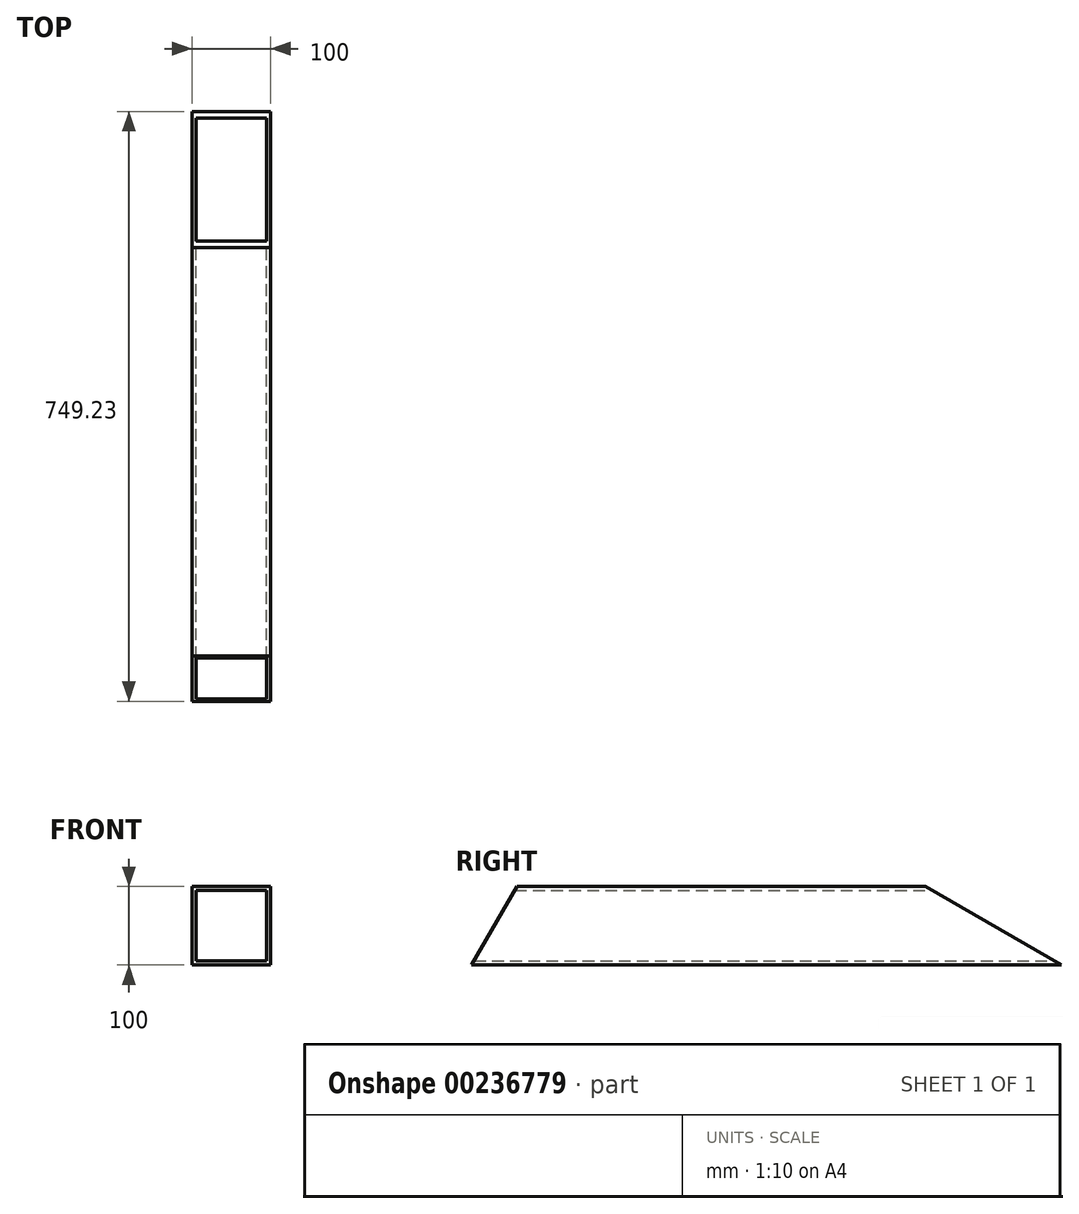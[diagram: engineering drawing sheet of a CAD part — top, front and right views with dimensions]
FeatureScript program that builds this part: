
annotation { "Feature Type Name" : "Feature", "Feature Type Description" : "" }
export const myFeature = defineFeature(function(context is Context, id is Id, definition is map)
    precondition{}
    {
        {
            var Q0;
            Q0=qCreatedBy(makeId("Front.planeOp"),FACE);
            var sketch = newSketch(context, id + "F0", { "sketchPlane" : qUnion([Q0])});
            skLineSegment(sketch, "E0.bottom", {"start": v(0, 0) * mm, "end": v(100, 0) * mm});
            skLineSegment(sketch, "E0.top", {"start": v(0, 100) * mm, "end": v(100, 100) * mm});
            skLineSegment(sketch, "E0.left", {"start": v(0, 0) * mm, "end": v(0, 100) * mm});
            skLineSegment(sketch, "E0.right", {"start": v(100, 0) * mm, "end": v(100, 100) * mm});
            skLineSegment(sketch, "E1.bottom", {"start": v(5, 95) * mm, "end": v(95, 95) * mm});
            skLineSegment(sketch, "E1.top", {"start": v(5, 5) * mm, "end": v(95, 5) * mm});
            skLineSegment(sketch, "E1.left", {"start": v(5, 95) * mm, "end": v(5, 5) * mm});
            skLineSegment(sketch, "E1.right", {"start": v(95, 95) * mm, "end": v(95, 5) * mm});
            skSolve(sketch);
        }
        {
            var Q0;
            Q0=makeQuery(id+"F0.imprint","IMPRINT",FACE,{"disambiguationData":[TD([[makeQuery(id+"F0.imprint","IMPRINT",EDGE,{"derivedFrom":sQuery(id+"F0.wireOp",EDGE,"E0.bottom")}),1.0]])]});
            extrude(context, id + "F1", {"entities" : qUnion([Q0]), "depth" : 750 * mm, "offsetDistance" : 25 * mm});
        }
        {
            var Q0;
            Q0=makeQuery(id+"F1.opExtrude","SWEPT_FACE",FACE,{"disambiguationData":[OSD([sQuery(id+"F0.wireOp",EDGE,"E0.right")])]});
            var sketch = newSketch(context, id + "F2", { "sketchPlane" : qUnion([Q0])});
            skLineSegment(sketch, "E2", {"start": v(-755, 120) * mm, "end": v(-679.94, 120) * mm});
            skLineSegment(sketch, "E3", {"start": v(-679.94, 120) * mm, "end": v(-755, -10) * mm});
            skLineSegment(sketch, "E4", {"start": v(-755, -10) * mm, "end": v(-755, 120) * mm});
            skSolve(sketch);
        }
        {
            var Q0;
            Q0 = qSketchRegion(id + "F2", true);
            extrude(context, id + "F3", {"entities" : qUnion([Q0]), "operationType" : NewBodyOperationType.REMOVE, "endBound" : BoundingType.THROUGH_ALL, "oppositeDirection" : true, "depth" : 25 * mm, "offsetDistance" : 25 * mm});
        }
        {
            var Q0;
            Q0=makeQuery(id+"F1.opExtrude","SWEPT_FACE",FACE,{"disambiguationData":[OSD([sQuery(id+"F0.wireOp",EDGE,"E0.right")])]});
            var sketch = newSketch(context, id + "F4", { "sketchPlane" : qUnion([Q0])});
            skLineSegment(sketch, "E5", {"start": v(-197.54, 114.15) * mm, "end": v(0.14, 0.02) * mm});
            skLineSegment(sketch, "E6", {"start": v(0.14, 0.02) * mm, "end": v(0.14, 114.15) * mm});
            skLineSegment(sketch, "E7", {"start": v(0.14, 114.15) * mm, "end": v(-197.54, 114.15) * mm});
            skSolve(sketch);
        }
        {
            var Q0;
            Q0 = qSketchRegion(id + "F4", true);
            extrude(context, id + "F5", {"entities" : qUnion([Q0]), "operationType" : NewBodyOperationType.REMOVE, "endBound" : BoundingType.THROUGH_ALL, "oppositeDirection" : true, "depth" : 25 * mm, "offsetDistance" : 25 * mm});
        }
    });
